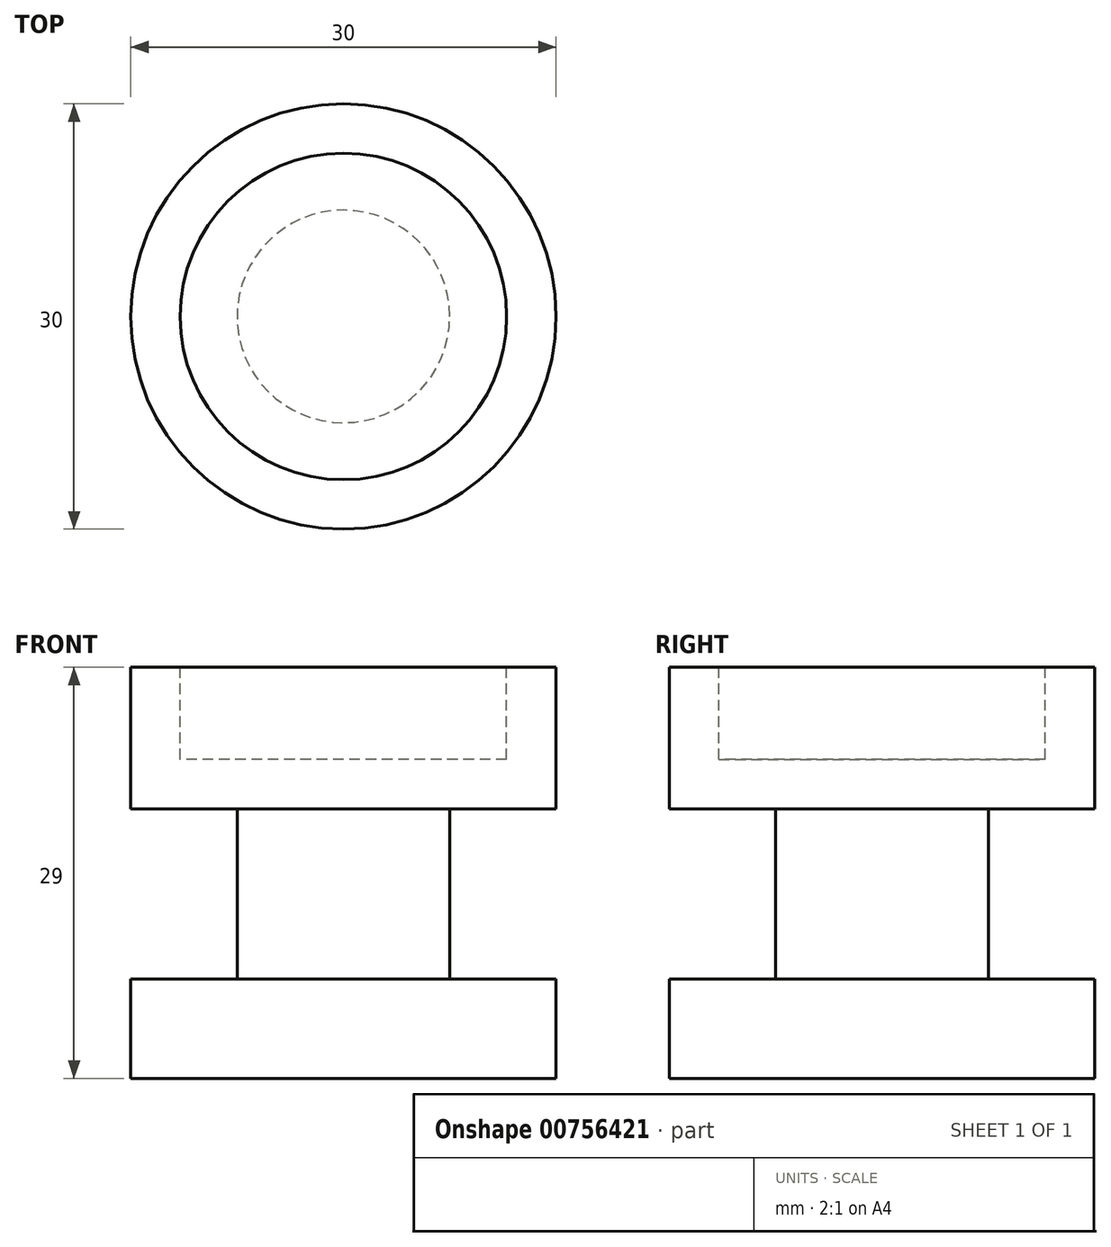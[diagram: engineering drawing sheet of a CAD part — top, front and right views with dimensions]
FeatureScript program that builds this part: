
annotation { "Feature Type Name" : "Feature", "Feature Type Description" : "" }
export const myFeature = defineFeature(function(context is Context, id is Id, definition is map)
    precondition{}
    {
        {
            var Q0;
            Q0=qCreatedBy(makeId("Front.planeOp"),FACE);
            var sketch = newSketch(context, id + "F0", { "sketchPlane" : qUnion([Q0])});
            skLineSegment(sketch, "E0.bottom", {"start": v(0, 0) * mm, "end": v(15, 0) * mm});
            skLineSegment(sketch, "E0.right", {"start": v(15, 0) * mm, "end": v(15, 7) * mm});
            skPoint(sketch, "E1.oppositeSnap0", {"position": v(7.5, 7) * mm});
            skLineSegment(sketch, "E1.right", {"start": v(7.5, 7) * mm, "end": v(7.5, 19) * mm});
            skLineSegment(sketch, "E2.top", {"start": v(0, 29) * mm, "end": v(15, 29) * mm});
            skLineSegment(sketch, "E2.right", {"start": v(15, 19) * mm, "end": v(15, 29) * mm});
            skLineSegment(sketch, "E3", {"start": v(7.5, 19) * mm, "end": v(15, 19) * mm});
            skLineSegment(sketch, "E4", {"start": v(7.5, 7) * mm, "end": v(15, 7) * mm});
            skLineSegment(sketch, "E5", {"start": v(0, 29) * mm, "end": v(0, 0) * mm});
            skSolve(sketch);
        }
        {
            var Q0;
            Q0 = qSketchRegion(id + "F0", true);
            var Q1;
            Q1=sQuery(id+"F0.wireOp",EDGE,"E5");
            revolve(context, id + "F1", {"surfaceOperationType" : NewSurfaceOperationType.NEW, "entities" : qUnion([Q0]), "axis" : qUnion([Q1]), "revolveType" : RevolveType.FULL});
        }
        {
            var Q0;
            Q0=makeQuery(id+"F1.opRevolve","SWEPT_FACE",FACE,{"disambiguationData":[OSD([sQuery(id+"F0.wireOp",EDGE,"E2.top")])]});
            var sketch = newSketch(context, id + "F2", { "sketchPlane" : qUnion([Q0])});
            skCircle(sketch, "E6", {"center": v(0, 0) * mm, "radius": 11.52 * mm});
            skSolve(sketch);
        }
        {
            var Q0;
            Q0=makeQuery(id+"F2.imprint","IMPRINT",FACE,{"disambiguationData":[TD([[makeQuery(id+"F2.imprint","IMPRINT",EDGE,{"derivedFrom":sQuery(id+"F2.wireOp",EDGE,"E6")}),1.0]])]});
            extrude(context, id + "F3", {"entities" : qUnion([Q0]), "operationType" : NewBodyOperationType.REMOVE, "oppositeDirection" : true, "depth" : 6.5 * mm, "offsetDistance" : 25 * mm});
        }
    });
